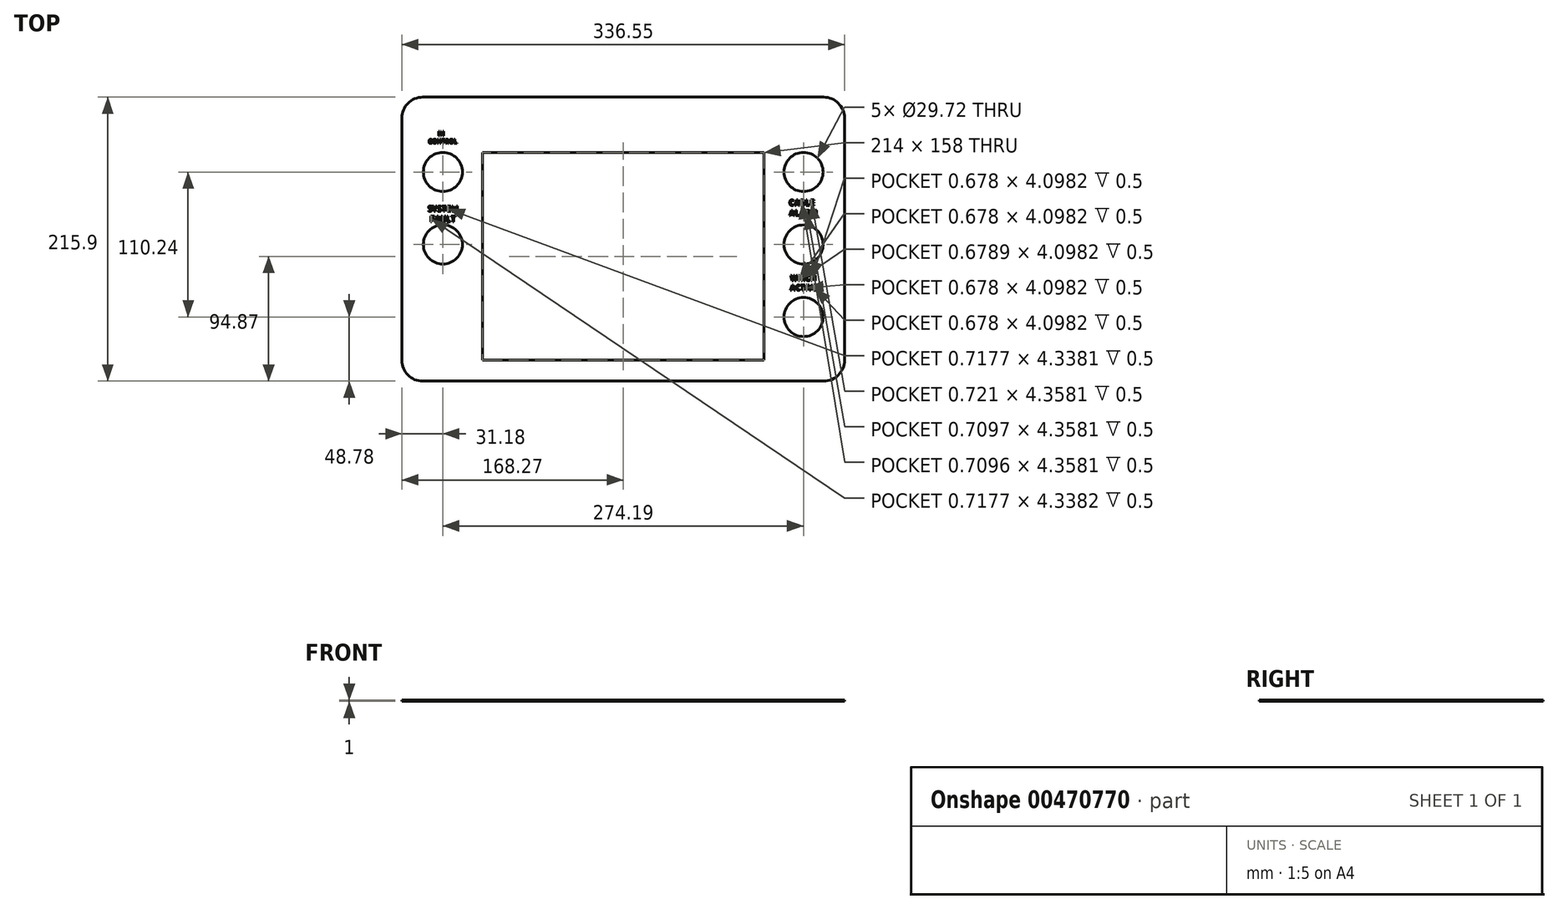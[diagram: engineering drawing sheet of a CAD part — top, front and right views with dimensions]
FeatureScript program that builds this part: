
annotation { "Feature Type Name" : "Feature", "Feature Type Description" : "" }
export const myFeature = defineFeature(function(context is Context, id is Id, definition is map)
    precondition{}
    {
        {
            var Q0;
            Q0=qCreatedBy(makeId("Top.planeOp"),FACE);
            var sketch = newSketch(context, id + "F0", { "sketchPlane" : qUnion([Q0])});
            skLineSegment(sketch, "E0.bottom", {"start": v(0, 0) * mm, "end": v(336.55, 0) * mm});
            skLineSegment(sketch, "E0.top", {"start": v(0, 215.9) * mm, "end": v(336.55, 215.9) * mm});
            skLineSegment(sketch, "E0.left", {"start": v(0, 0) * mm, "end": v(0, 215.9) * mm});
            skLineSegment(sketch, "E0.right", {"start": v(336.55, 0) * mm, "end": v(336.55, 215.9) * mm});
            skSolve(sketch);
        }
        {
            var Q0;
            Q0=makeQuery(id+"F0.imprint","IMPRINT",FACE,{"disambiguationData":[TD([[makeQuery(id+"F0.imprint","IMPRINT",EDGE,{"derivedFrom":sQuery(id+"F0.wireOp",EDGE,"E0.bottom")}),1.0]])]});
            extrude(context, id + "F1", {"entities" : qUnion([Q0]), "depth" : 1 * mm});
        }
        {
            var Q0;
            Q0=makeQuery(id+"F1.opExtrude","SWEPT_EDGE",EDGE,{"disambiguationData":[OSD([sQuery(id+"F0.wireOp",EDGE,"E0.bottom"),sQuery(id+"F0.wireOp",EDGE,"E0.right")])]});
            var Q1;
            Q1=makeQuery(id+"F1.opExtrude","SWEPT_EDGE",EDGE,{"disambiguationData":[OSD([sQuery(id+"F0.wireOp",EDGE,"E0.top"),sQuery(id+"F0.wireOp",EDGE,"E0.right")])]});
            var Q2;
            Q2=makeQuery(id+"F1.opExtrude","SWEPT_EDGE",EDGE,{"disambiguationData":[OSD([sQuery(id+"F0.wireOp",EDGE,"E0.bottom"),sQuery(id+"F0.wireOp",EDGE,"E0.left")])]});
            var Q3;
            Q3=makeQuery(id+"F1.opExtrude","SWEPT_EDGE",EDGE,{"disambiguationData":[OSD([sQuery(id+"F0.wireOp",EDGE,"E0.top"),sQuery(id+"F0.wireOp",EDGE,"E0.left")])]});
            fillet(context, id + "F2", {"entities" : qUnion([Q0, Q1, Q2, Q3]), "radius" : 15.88 * mm, "tangentPropagation" : true, "allowEdgeOverflow" : false});
        }
        {
            var Q0;
            Q0=makeQuery(id+"F1.opExtrude","CAP_FACE",FACE,{"disambiguationData":[OSD([sQuery(id+"F0.wireOp",EDGE,"E0.bottom"),sQuery(id+"F0.wireOp",EDGE,"E0.top"),sQuery(id+"F0.wireOp",EDGE,"E0.left"),sQuery(id+"F0.wireOp",EDGE,"E0.right")])],"isStart":false});
            var sketch = newSketch(context, id + "F3", { "sketchPlane" : qUnion([Q0])});
            skLineSegment(sketch, "E1.bottom", {"start": v(61.27, 173.87) * mm, "end": v(275.27, 173.87) * mm});
            skLineSegment(sketch, "E1.top", {"start": v(61.27, 15.87) * mm, "end": v(275.27, 15.87) * mm});
            skLineSegment(sketch, "E1.left", {"start": v(61.27, 173.87) * mm, "end": v(61.27, 15.87) * mm});
            skLineSegment(sketch, "E1.right", {"start": v(275.27, 173.87) * mm, "end": v(275.27, 15.87) * mm});
            skCircle(sketch, "E2", {"center": v(31.18, 159.02) * mm, "radius": 14.86 * mm});
            skCircle(sketch, "E3", {"center": v(31.18, 103.9) * mm, "radius": 14.86 * mm});
            skCircle(sketch, "E4", {"center": v(305.37, 159.02) * mm, "radius": 14.86 * mm});
            skCircle(sketch, "E5", {"center": v(305.37, 103.9) * mm, "radius": 14.86 * mm});
            skCircle(sketch, "E6", {"center": v(305.37, 48.78) * mm, "radius": 14.86 * mm});
            skSolve(sketch);
        }
        {
            var Q0;
            Q0 = qSketchRegion(id + "F3", true);
            extrude(context, id + "F4", {"entities" : qUnion([Q0]), "operationType" : NewBodyOperationType.REMOVE, "endBound" : BoundingType.THROUGH_ALL, "oppositeDirection" : true, "depth" : 25 * mm});
        }
        {
            var Q0;
            Q0=makeQuery(id+"F1.opExtrude","CAP_FACE",FACE,{"disambiguationData":[OSD([sQuery(id+"F0.wireOp",EDGE,"E0.bottom"),sQuery(id+"F0.wireOp",EDGE,"E0.top"),sQuery(id+"F0.wireOp",EDGE,"E0.left"),sQuery(id+"F0.wireOp",EDGE,"E0.right")])],"isStart":false});
            var sketch = newSketch(context, id + "F5", { "sketchPlane" : qUnion([Q0])});
            skText(sketch, "E7", { "text": "      IN\nCONTROL", "fontName": "AllertaStencil-Regular.ttf"});
            skText(sketch, "E8", { "text": "SYSTEM\n FAULT", "fontName": "AllertaStencil-Regular.ttf"});
            skText(sketch, "E9", { "text": "CABLE\nALARM", "fontName": "AllertaStencil-Regular.ttf"});
            skText(sketch, "E10", { "text": "WINCH\nACTIVE", "fontName": "AllertaStencil-Regular.ttf"});
            const initialGuessF5  = {"E7": [0.0202, 0.18659, 1, 0, 0.00333], "E8": [0.01982, 0.1289, 1, 0, 0.00434], "E9": [0.29433, 0.1335, 1, 0, 0.00436], "E10": [0.2951, 0.0763, 1, 0, 0.0041]};
            skSetInitialGuess(sketch, initialGuessF5);
            skSolve(sketch);
        }
        {
            var Q0;
            Q0 = qSketchRegion(id + "F5", true);
            extrude(context, id + "F6", {"entities" : qUnion([Q0]), "operationType" : NewBodyOperationType.REMOVE, "oppositeDirection" : true, "depth" : 0.5 * mm});
        }
    });
